# Revit family: STS-507 Контроллер связи
name_source: partatom
category: Электрооборудование
revit_build: Autodesk Revit 2017 (Build: 20170118_1100(x64)
units: mm (PartAtom-declared; Revit-internal decimal feet)

## family parameters
Всегда вертикально = Нет
Конфигурация панели = Два столбца, слева направо
На основе рабочей плоскости = Да
Общий = Нет
При загрузке вырезать с полостями = Нет
Размер круглого соединителя = Использовать диаметр
Тип детали = Щит
Точка расчета площади = Нет

## types (1)
- STS-507
    ADSK_URL страницы изделия = https://stilsoft.ru
    ADSK_Единица измерения = шт.
    ADSK_Завод-изготовитель = ООО «Основа Безопасности»
    ADSK_Количество = 1
    ADSK_Марка = CТАЕ.424252.037
    ADSK_Масса = 2
    ADSK_Наименование = Контроллер связи STS-507
    ADSK_Размер_Высота = 300 мм
    ADSK_Размер_Глубина = 97 мм
    ADSK_Размер_Ширина = 225 мм
    d_короба = 0 мм
    Вариант исполнения = уличный
    Время непрерывной работы, ч = круглосуточно
    Диапазон рабочих температур, °С = от -40 до +50
    Интерфейс (тип) = Ethernet (10/100BaseT)
    Используемые полосы частот, МГц = 5150–5350
    Кадрирование / Кодирование = IEEE 802.3/U
    Максимальная мощность передатчика, дБм = 20
    Максимальная потребляемая мощность, не более, Вт = 30
    Мощность = 30
    Напряжение = 12
    Напряжение электропитания постоянного тока, В = 12-24
    Отметка по умолчанию = 1219 мм
    Полоса пропускания канала, МГ = 20, 40
    Скорость передачи данных, до Мбит/с = 40
